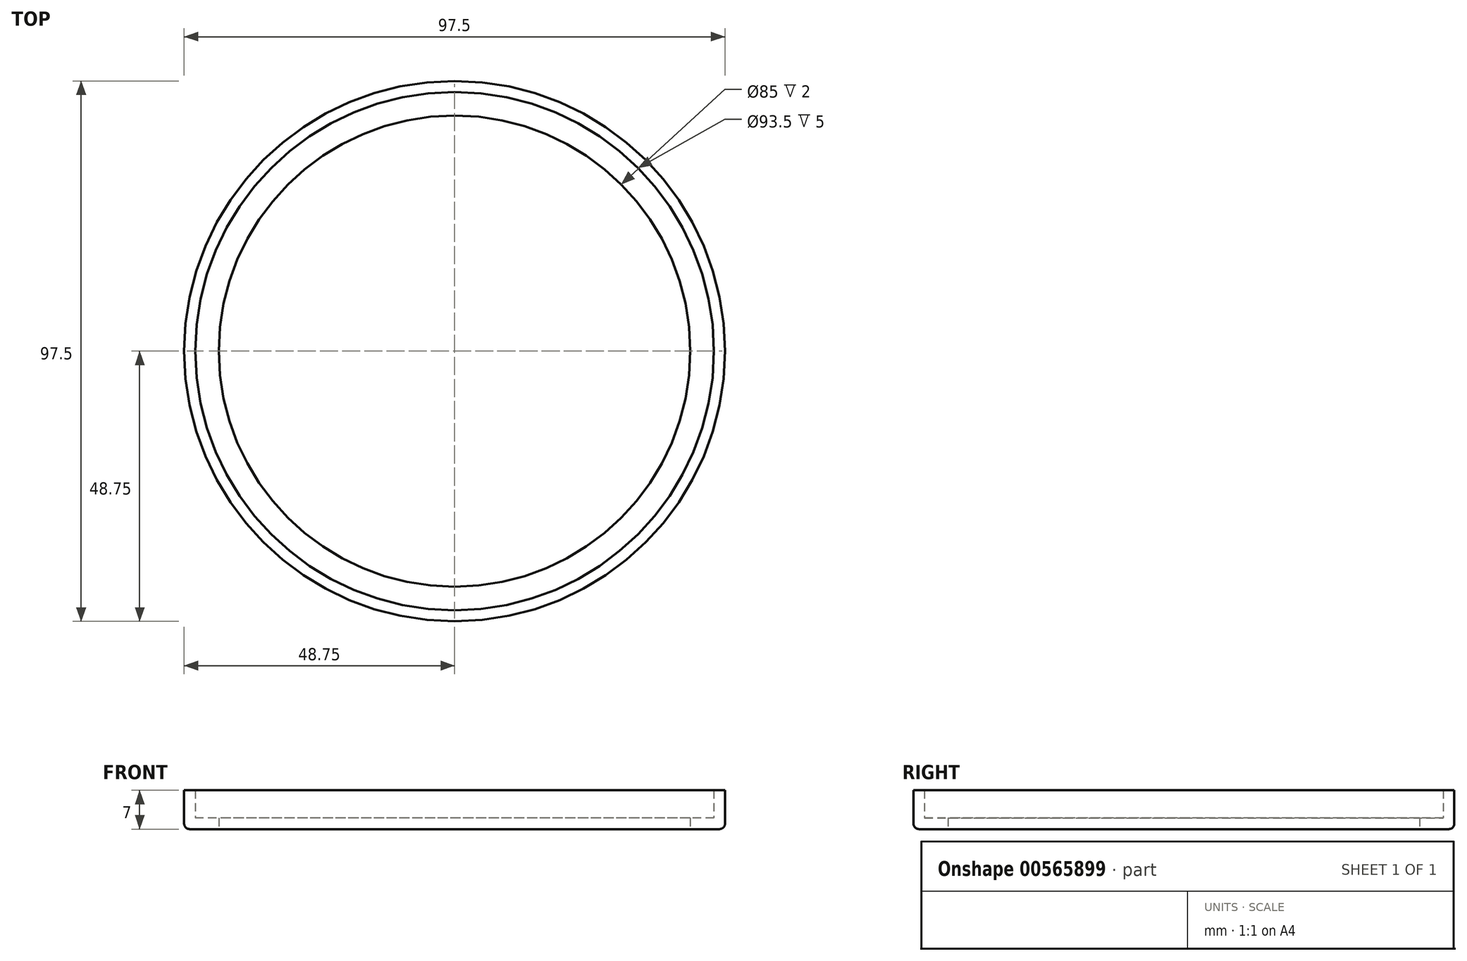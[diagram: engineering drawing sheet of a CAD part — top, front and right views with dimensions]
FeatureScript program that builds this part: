
annotation { "Feature Type Name" : "Feature", "Feature Type Description" : "" }
export const myFeature = defineFeature(function(context is Context, id is Id, definition is map)
    precondition{}
    {
        {
            var Q0;
            Q0=qCreatedBy(makeId("Top.planeOp"),FACE);
            var sketch = newSketch(context, id + "F0", { "sketchPlane" : qUnion([Q0])});
            skCircle(sketch, "E0", {"center": v(0, 0) * mm, "radius": 48.75 * mm});
            skCircle(sketch, "E1", {"center": v(0, 0) * mm, "radius": 42.5 * mm});
            skSolve(sketch);
        }
        {
            var Q0;
            Q0=makeQuery(id+"F0.imprint","IMPRINT",FACE,{"disambiguationData":[TD([[makeQuery(id+"F0.imprint","IMPRINT",EDGE,{"derivedFrom":sQuery(id+"F0.wireOp",EDGE,"E0")}),1.0]])]});
            extrude(context, id + "F1", {"entities" : qUnion([Q0]), "depth" : 2 * mm, "offsetDistance" : 25 * mm});
        }
        {
            var Q0;
            Q0=makeQuery(id+"F1.opExtrude","CAP_FACE",FACE,{"disambiguationData":[OSD([sQuery(id+"F0.wireOp",EDGE,"E0"),sQuery(id+"F0.wireOp",EDGE,"E1")])],"isStart":false});
            var sketch = newSketch(context, id + "F2", { "sketchPlane" : qUnion([Q0])});
            skCircle(sketch, "E2.0", {"center": v(0, 0) * mm, "radius": 46.75 * mm});
            skCircle(sketch, "E3.0", {"center": v(0, 0) * mm, "radius": 48.75 * mm});
            skSolve(sketch);
        }
        {
            var Q0;
            Q0=makeQuery(id+"F2.imprint","IMPRINT",FACE,{"disambiguationData":[TD([[makeQuery(id+"F2.imprint","IMPRINT",EDGE,{"derivedFrom":sQuery(id+"F2.wireOp",EDGE,"E2.0")}),-1.0]])]});
            extrude(context, id + "F3", {"entities" : qUnion([Q0]), "operationType" : NewBodyOperationType.ADD, "depth" : 5 * mm, "offsetDistance" : 25 * mm});
        }
        {
            var Q0;
            Q0=makeQuery(id+"F1.opExtrude","CAP_EDGE",EDGE,{"disambiguationData":[OSD([sQuery(id+"F0.wireOp",EDGE,"E0")])],"isStart":true});
            fillet(context, id + "F4", {"entities" : qUnion([Q0]), "radius" : 1 * mm, "tangentPropagation" : true, "allowEdgeOverflow" : false});
        }
    });
